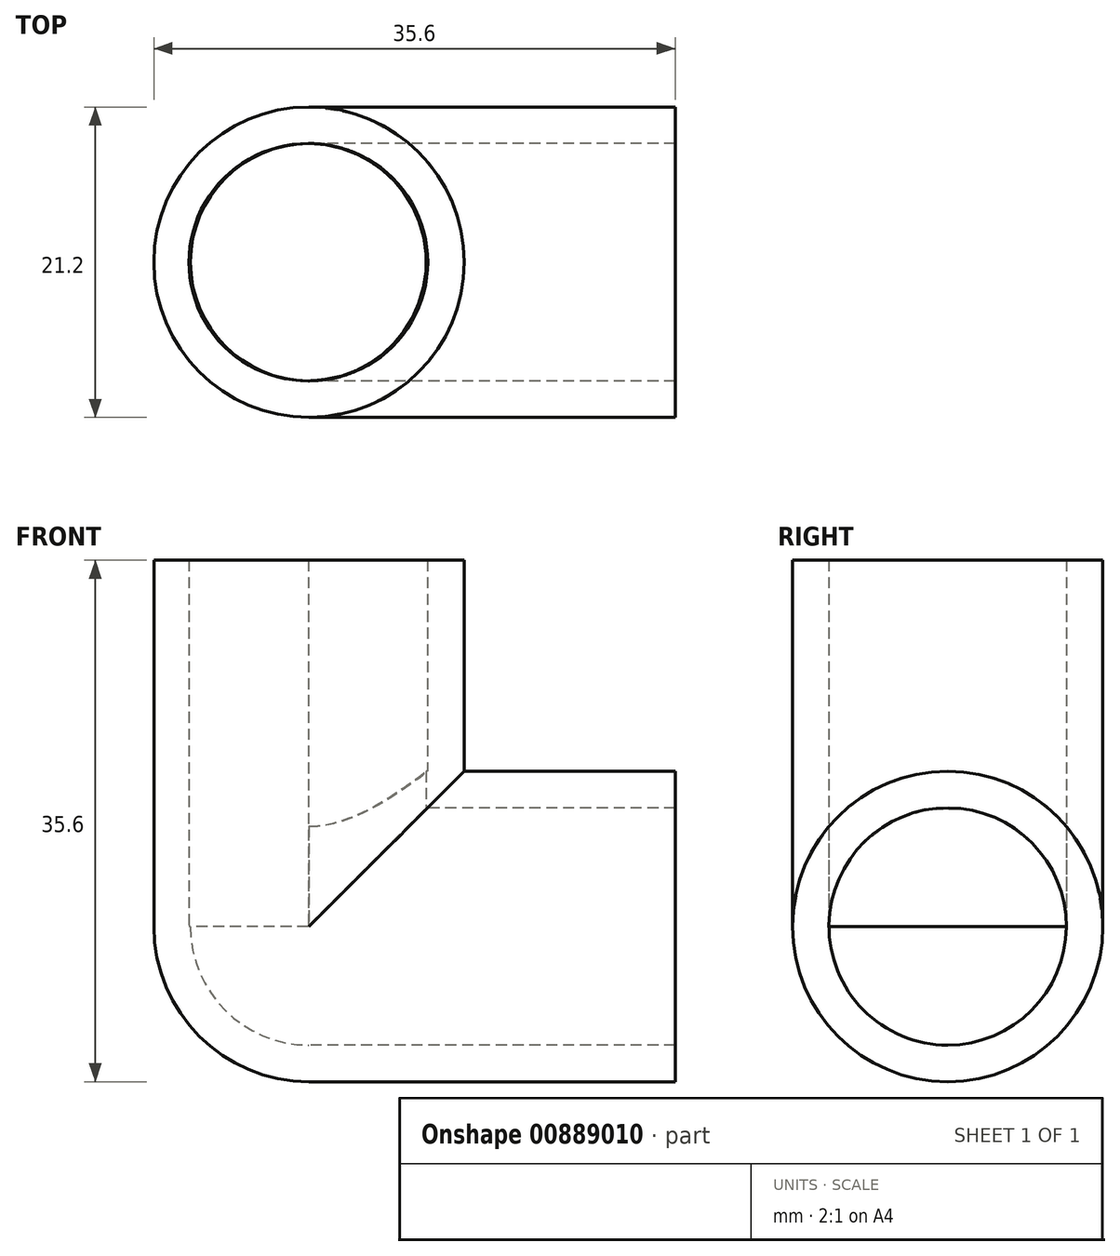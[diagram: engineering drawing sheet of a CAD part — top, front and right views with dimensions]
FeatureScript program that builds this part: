
annotation { "Feature Type Name" : "Feature", "Feature Type Description" : "" }
export const myFeature = defineFeature(function(context is Context, id is Id, definition is map)
    precondition{}
    {
        {
            var Q0;
            Q0=qCreatedBy(makeId("Top.planeOp"),FACE);
            var sketch = newSketch(context, id + "F0", { "sketchPlane" : qUnion([Q0])});
            skCircle(sketch, "E0", {"center": v(0, 0) * mm, "radius": 8.1 * mm});
            skCircle(sketch, "E1.0", {"center": v(-0.1, 0) * mm, "radius": 8.1 * mm});
            skCircle(sketch, "E2.0", {"center": v(0, 0) * mm, "radius": 10.6 * mm});
            skSolve(sketch);
        }
        {
            var Q0;
            Q0=makeQuery(id+"F0.imprint","IMPRINT",FACE,{"disambiguationData":[TD([[makeQuery(id+"F0.imprint","IMPRINT",EDGE,{"derivedFrom":sQuery(id+"F0.wireOp",EDGE,"E2.0")}),1.0]])]});
            extrude(context, id + "F1", {"entities" : qUnion([Q0]), "depth" : 25 * mm, "offsetDistance" : 25 * mm});
        }
        {
            var Q0;
            Q0=qCreatedBy(makeId("Right.planeOp"),FACE);
            var sketch = newSketch(context, id + "F2", { "sketchPlane" : qUnion([Q0])});
            skCircle(sketch, "E3", {"center": v(0, 0) * mm, "radius": 8.1 * mm});
            skCircle(sketch, "E4.0", {"center": v(0, 0) * mm, "radius": 10.6 * mm});
            skSolve(sketch);
        }
        {
            var Q0;
            Q0=makeQuery(id+"F2.imprint","IMPRINT",FACE,{"disambiguationData":[TD([[makeQuery(id+"F2.imprint","IMPRINT",EDGE,{"derivedFrom":sQuery(id+"F2.wireOp",EDGE,"E3")}),-1.0]])]});
            var Q1;
            Q1=makeQuery(id+"F1.opExtrude","SWEPT_BODY",BODY,{"disambiguationData":[OSD([sQuery(id+"F0.wireOp",EDGE,"E1.0"),sQuery(id+"F0.wireOp",EDGE,"E2.0")])]});
            extrude(context, id + "F3", {"entities" : qUnion([Q0]), "operationType" : NewBodyOperationType.ADD, "depth" : 25 * mm, "endBoundEntityBody" : qUnion([Q1]), "offsetDistance" : 25 * mm});
        }
        {
            var Q0;
            Q0=makeQuery(id+"F0.imprint","IMPRINT",FACE,{"disambiguationData":[TD([[makeQuery(id+"F0.imprint","IMPRINT",EDGE,{"derivedFrom":sQuery(id+"F0.wireOp",EDGE,"E1.0")}),1.0]])]});
            extrude(context, id + "F4", {"entities" : qUnion([Q0]), "operationType" : NewBodyOperationType.REMOVE, "depth" : 15 * mm, "offsetDistance" : 25 * mm});
        }
        {
            var Q0;
            Q0=makeQuery(id+"F2.imprint","IMPRINT",FACE,{"disambiguationData":[TD([[makeQuery(id+"F2.imprint","IMPRINT",EDGE,{"derivedFrom":sQuery(id+"F2.wireOp",EDGE,"E3")}),1.0]])]});
            extrude(context, id + "F5", {"entities" : qUnion([Q0]), "operationType" : NewBodyOperationType.REMOVE, "depth" : 25 * mm, "offsetDistance" : 25 * mm});
        }
        {
            var Q0;
            Q0=makeQuery(id+"F2.imprint","IMPRINT",FACE,{"disambiguationData":[TD([[makeQuery(id+"F2.imprint","IMPRINT",EDGE,{"derivedFrom":sQuery(id+"F2.wireOp",EDGE,"E3")}),-1.0]])]});
            var sketch = newSketch(context, id + "F6", { "sketchPlane" : qUnion([Q0])});
            skCircle(sketch, "E5", {"center": v(0, 0) * mm, "radius": 8.1 * mm});
            skCircle(sketch, "E6", {"center": v(0, 0) * mm, "radius": 10.6 * mm});
            skLineSegment(sketch, "E7", {"start": v(8.1, 0) * mm, "end": v(10.6, 0) * mm});
            skLineSegment(sketch, "E8", {"start": v(-8.1, 0) * mm, "end": v(-10.6, 0) * mm});
            skSolve(sketch);
        }
        {
            var Q0;
            Q0=qCreatedBy(makeId("Front.planeOp"),FACE);
            var sketch = newSketch(context, id + "F7", { "sketchPlane" : qUnion([Q0])});
            skCircle(sketch, "E9", {"center": v(0, 0) * mm, "radius": 12.89 * mm});
            skSolve(sketch);
        }
        {
            var Q0;
            {var subQ0=sQuery(id+"F6.wireOp",EDGE,"E7");Q0=makeQuery(id+"F6.imprint","IMPRINT",FACE,{"disambiguationData":[TD([[makeQuery(id+"F6.imprint","IMPRINT",EDGE,{"derivedFrom":subQ0}),-1.0]])]});}
            var Q1;
            Q1=sQuery(id+"F7.wireOp",EDGE,"E9");
            revolve(context, id + "F8", {"operationType" : NewBodyOperationType.ADD, "surfaceOperationType" : NewSurfaceOperationType.NEW, "entities" : qUnion([Q0]), "axis" : qUnion([Q1]), "revolveType" : RevolveType.ONE_DIRECTION, "oppositeDirection" : true, "angle" : 90 * degree});
        }
    });
